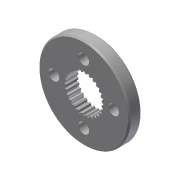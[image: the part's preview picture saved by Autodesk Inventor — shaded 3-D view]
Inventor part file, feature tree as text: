
AUTODESK INVENTOR PART (.ipt)
format: ipt  version: 2013 (Build 170138000, 138)  size: 214,528 bytes
history: native  units: in
note: dims shown in document units (in); Inventor stores cm internally (conversion verified against a paired STEP export)
features: chamfer x1, other x1, imported_body x1
ambient origin geometry x8: Origin, YZ Plane, XZ Plane, XY Plane, X Axis, Y Axis, Z Axis, Center Point
feature tree (3):
  chamfer  "Chamfer1"  [1 undecoded]
  other  "217-2726-002 Rev11"
  imported_body  "Base1"
note: 1 required parameter value undecoded (feature->parameter linkage not recoverable at this tier; creation-order binding heuristic only, values carry confidence <= 0.55)
